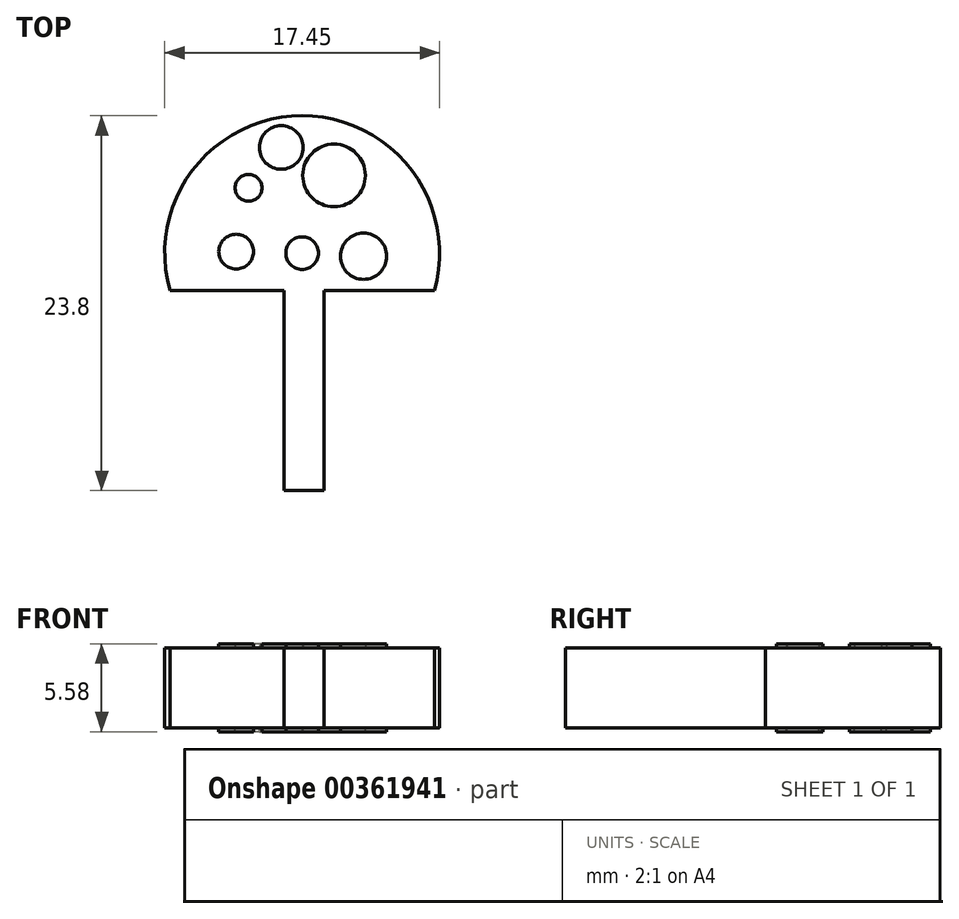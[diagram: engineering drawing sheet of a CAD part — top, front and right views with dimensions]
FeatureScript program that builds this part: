
annotation { "Feature Type Name" : "Feature", "Feature Type Description" : "" }
export const myFeature = defineFeature(function(context is Context, id is Id, definition is map)
    precondition{}
    {
        {
            var Q0;
            Q0=qCreatedBy(makeId("Top.planeOp"),FACE);
            var sketch = newSketch(context, id + "F0", { "sketchPlane" : qUnion([Q0])});
            skPoint(sketch, "E0.middle", {"position": v(0, 0) * mm});
            skLineSegment(sketch, "E1.bottom", {"start": v(-1.27, -6.35) * mm, "end": v(1.27, -6.35) * mm});
            skLineSegment(sketch, "E1.top", {"start": v(-1.27, 6.35) * mm, "end": v(1.27, 6.35) * mm});
            skLineSegment(sketch, "E1.left", {"start": v(-1.27, -6.35) * mm, "end": v(-1.27, 6.35) * mm});
            skLineSegment(sketch, "E1.right", {"start": v(1.27, -6.35) * mm, "end": v(1.27, 6.35) * mm});
            skLineSegment(sketch, "E2", {"start": v(-1.27, 6.35) * mm, "end": v(-8.52, 6.35) * mm});
            skLineSegment(sketch, "E3", {"start": v(1.27, 6.35) * mm, "end": v(8.27, 6.35) * mm});
            skArc(sketch, "E4", {"start": v(-1.27, 0.07) * mm, "mid": v(0, 0) * mm, "end": v(1.27, 0.11) * mm});
            skPoint(sketch, "E4.second.point", {"position": v(0, 17.45) * mm});
            skArc(sketch, "E5.trimOffspring", {"start": v(8.27, 6.35) * mm, "mid": v(-0.13, 17.45) * mm, "end": v(-8.52, 6.35) * mm});
            skSolve(sketch);
        }
        {
            var Q0;
            Q0 = qSketchRegion(id + "F0", true);
            extrude(context, id + "F1", {"entities" : qUnion([Q0]), "depth" : 2.54 * mm});
        }
        {
            var Q0;
            Q0=makeQuery(id+"F1.opExtrude","CAP_FACE",FACE,{"disambiguationData":[OSD([sQuery(id+"F0.wireOp",EDGE,"E1.bottom"),sQuery(id+"F0.wireOp",EDGE,"E1.left"),sQuery(id+"F0.wireOp",EDGE,"E1.right"),sQuery(id+"F0.wireOp",EDGE,"E2"),sQuery(id+"F0.wireOp",EDGE,"E3"),sQuery(id+"F0.wireOp",EDGE,"E5.trimOffspring")])],"isStart":false});
            var sketch = newSketch(context, id + "F2", { "sketchPlane" : qUnion([Q0])});
            skCircle(sketch, "E6", {"center": v(-3.53, 12.87) * mm, "radius": 0.85 * mm});
            skCircle(sketch, "E7", {"center": v(3.78, 8.52) * mm, "radius": 1.47 * mm});
            skCircle(sketch, "E8", {"center": v(1.9, 13.66) * mm, "radius": 1.99 * mm});
            skCircle(sketch, "E9", {"center": v(-4.32, 8.82) * mm, "radius": 1.1 * mm});
            skCircle(sketch, "E10", {"center": v(-0.13, 8.72) * mm, "radius": 1.04 * mm});
            skCircle(sketch, "E11", {"center": v(-1.46, 15.43) * mm, "radius": 1.39 * mm});
            skSolve(sketch);
        }
        {
            var Q0;
            Q0 = qSketchRegion(id + "F2", true);
            extrude(context, id + "F3", {"entities" : qUnion([Q0]), "operationType" : NewBodyOperationType.ADD, "depth" : 0.25 * mm});
        }
        {
            var Q0;
            Q0=makeQuery(id+"F1.opExtrude","SWEPT_BODY",BODY,{"disambiguationData":[OSD([sQuery(id+"F0.wireOp",EDGE,"E1.bottom"),sQuery(id+"F0.wireOp",EDGE,"E1.left"),sQuery(id+"F0.wireOp",EDGE,"E1.right"),sQuery(id+"F0.wireOp",EDGE,"E2"),sQuery(id+"F0.wireOp",EDGE,"E3"),sQuery(id+"F0.wireOp",EDGE,"E5.trimOffspring")])]});
            var Q1;
            Q1=qCreatedBy(makeId("Top.planeOp"),FACE);
            mirror(context, id + "F4", {"operationType" : NewBodyOperationType.ADD, "entities" : qUnion([Q0]), "mirrorPlane" : qUnion([Q1])});
        }
    });
